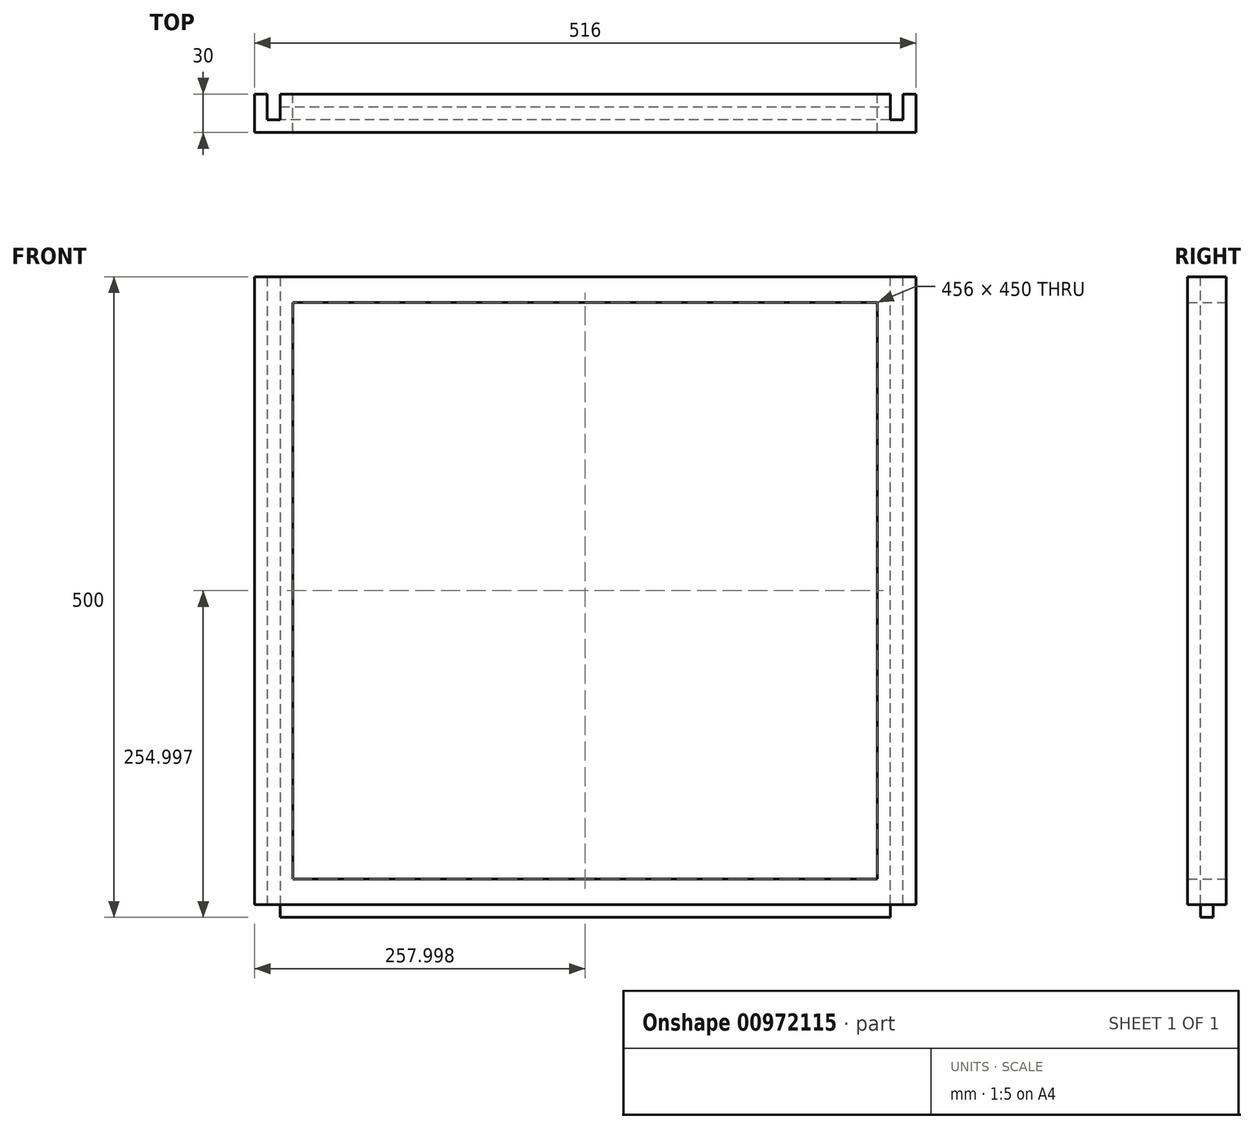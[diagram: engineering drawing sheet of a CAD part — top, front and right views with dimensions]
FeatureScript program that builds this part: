
annotation { "Feature Type Name" : "Feature", "Feature Type Description" : "" }
export const myFeature = defineFeature(function(context is Context, id is Id, definition is map)
    precondition{}
    {
        {
            var Q0;
            Q0=qCreatedBy(makeId("Front.planeOp"),FACE);
            var sketch = newSketch(context, id + "F0", { "sketchPlane" : qUnion([Q0])});
            skLineSegment(sketch, "E0.bottom", {"start": v(-276.65, 302.68) * mm, "end": v(259.35, 302.68) * mm});
            skLineSegment(sketch, "E0.top", {"start": v(-276.65, -197.32) * mm, "end": v(259.35, -197.32) * mm});
            skLineSegment(sketch, "E0.left", {"start": v(-276.65, 302.68) * mm, "end": v(-276.65, -197.32) * mm});
            skLineSegment(sketch, "E0.right", {"start": v(259.35, 302.68) * mm, "end": v(259.35, -197.32) * mm});
            skLineSegment(sketch, "E1.bottom", {"start": v(-236.65, -167.32) * mm, "end": v(219.35, -167.32) * mm});
            skLineSegment(sketch, "E1.top", {"start": v(-236.65, 282.68) * mm, "end": v(219.35, 282.68) * mm});
            skLineSegment(sketch, "E1.left", {"start": v(-236.65, -167.32) * mm, "end": v(-236.65, 282.68) * mm});
            skLineSegment(sketch, "E1.right", {"start": v(219.35, -167.32) * mm, "end": v(219.35, 282.68) * mm});
            skSolve(sketch);
        }
        {
            var Q0;
            Q0 = qSketchRegion(id + "F0", true);
            extrude(context, id + "F1", {"entities" : qUnion([Q0]), "depth" : 20 * mm, "offsetDistance" : 25 * mm});
        }
        {
            var Q0;
            Q0=makeQuery(id+"F1.opExtrude","SWEPT_FACE",FACE,{"disambiguationData":[OSD([sQuery(id+"F0.wireOp",EDGE,"E0.left")])]});
            var sketch = newSketch(context, id + "F2", { "sketchPlane" : qUnion([Q0])});
            skLineSegment(sketch, "E2.bottom", {"start": v(20, -197.32) * mm, "end": v(10, -197.32) * mm});
            skLineSegment(sketch, "E2.top", {"start": v(20, -187.32) * mm, "end": v(10, -187.32) * mm});
            skLineSegment(sketch, "E2.left", {"start": v(20, -197.32) * mm, "end": v(20, -187.32) * mm});
            skLineSegment(sketch, "E2.right", {"start": v(10, -197.32) * mm, "end": v(10, -187.32) * mm});
            skSolve(sketch);
        }
        {
            var Q0;
            Q0 = qSketchRegion(id + "F2", true);
            extrude(context, id + "F3", {"entities" : qUnion([Q0]), "operationType" : NewBodyOperationType.REMOVE, "endBound" : BoundingType.UP_TO_NEXT, "oppositeDirection" : true, "depth" : 25 * mm, "offsetDistance" : 25 * mm});
        }
        {
            var Q0;
            Q0=makeQuery(id+"F1.opExtrude","CAP_FACE",FACE,{"disambiguationData":[OSD([sQuery(id+"F0.wireOp",EDGE,"E0.bottom"),sQuery(id+"F0.wireOp",EDGE,"E0.top"),sQuery(id+"F0.wireOp",EDGE,"E0.left"),sQuery(id+"F0.wireOp",EDGE,"E0.right"),sQuery(id+"F0.wireOp",EDGE,"E1.bottom"),sQuery(id+"F0.wireOp",EDGE,"E1.top"),sQuery(id+"F0.wireOp",EDGE,"E1.left"),sQuery(id+"F0.wireOp",EDGE,"E1.right")])],"isStart":true});
            var sketch = newSketch(context, id + "F4", { "sketchPlane" : qUnion([Q0])});
            skLineSegment(sketch, "E3.bottom", {"start": v(246.65, 302.68) * mm, "end": v(256.65, 302.68) * mm});
            skLineSegment(sketch, "E3.top", {"start": v(246.65, -197.32) * mm, "end": v(256.65, -197.32) * mm});
            skLineSegment(sketch, "E3.left", {"start": v(246.65, 302.68) * mm, "end": v(246.65, -197.32) * mm});
            skLineSegment(sketch, "E3.right", {"start": v(256.65, 302.68) * mm, "end": v(256.65, -197.32) * mm});
            skLineSegment(sketch, "E4.bottom", {"start": v(-239.35, -197.32) * mm, "end": v(-229.35, -197.32) * mm});
            skLineSegment(sketch, "E4.top", {"start": v(-239.35, 302.68) * mm, "end": v(-229.35, 302.68) * mm});
            skLineSegment(sketch, "E4.left", {"start": v(-239.35, -197.32) * mm, "end": v(-239.35, 302.68) * mm});
            skLineSegment(sketch, "E4.right", {"start": v(-229.35, -197.32) * mm, "end": v(-229.35, 302.68) * mm});
            skSolve(sketch);
        }
        {
            var Q0;
            Q0 = qSketchRegion(id + "F4", true);
            extrude(context, id + "F5", {"entities" : qUnion([Q0]), "operationType" : NewBodyOperationType.REMOVE, "oppositeDirection" : true, "depth" : 10 * mm, "offsetDistance" : 25 * mm});
        }
        {
            var Q0;
            Q0=makeQuery(id+"F1.opExtrude","SWEPT_FACE",FACE,{"disambiguationData":[OSD([sQuery(id+"F0.wireOp",EDGE,"E0.right")])]});
            var sketch = newSketch(context, id + "F6", { "sketchPlane" : qUnion([Q0])});
            skLineSegment(sketch, "E5.bottom", {"start": v(-10, -197.32) * mm, "end": v(-10, -197.32) * mm});
            skPoint(sketch, "E6.oppositeSnap0", {"position": v(-15, -187.32) * mm});
            skLineSegment(sketch, "E6.bottom", {"start": v(-10, -197.32) * mm, "end": v(0, -197.32) * mm});
            skLineSegment(sketch, "E6.top", {"start": v(-10, -187.32) * mm, "end": v(0, -187.32) * mm});
            skLineSegment(sketch, "E6.left", {"start": v(-10, -197.32) * mm, "end": v(-10, -187.32) * mm});
            skLineSegment(sketch, "E6.right", {"start": v(0, -197.32) * mm, "end": v(0, -187.32) * mm});
            skSolve(sketch);
        }
        {
            var Q0;
            Q0=makeQuery(id+"F6.imprint","IMPRINT",FACE,{"disambiguationData":[TD([[makeQuery(id+"F6.imprint","IMPRINT",EDGE,{"derivedFrom":sQuery(id+"F6.wireOp",EDGE,"E6.bottom")}),1.0]])]});
            extrude(context, id + "F7", {"entities" : qUnion([Q0]), "operationType" : NewBodyOperationType.REMOVE, "endBound" : BoundingType.UP_TO_NEXT, "oppositeDirection" : true, "depth" : 25 * mm, "offsetDistance" : 25 * mm});
        }
        {
            var Q0;
            Q0=makeQuery(id+"F1.opExtrude","SWEPT_FACE",FACE,{"disambiguationData":[OSD([sQuery(id+"F0.wireOp",EDGE,"E0.left")])]});
            var sketch = newSketch(context, id + "F8", { "sketchPlane" : qUnion([Q0])});
            skLineSegment(sketch, "E7.bottom", {"start": v(10, -197.32) * mm, "end": v(0, -197.32) * mm});
            skLineSegment(sketch, "E7.top", {"start": v(10, -187.32) * mm, "end": v(0, -187.32) * mm});
            skLineSegment(sketch, "E7.left", {"start": v(10, -197.32) * mm, "end": v(10, -187.32) * mm});
            skLineSegment(sketch, "E7.right", {"start": v(0, -197.32) * mm, "end": v(0, -187.32) * mm});
            skSolve(sketch);
        }
        {
            var Q0;
            Q0=makeQuery(id+"F8.imprint","IMPRINT",FACE,{"disambiguationData":[TD([[makeQuery(id+"F8.imprint","IMPRINT",EDGE,{"derivedFrom":sQuery(id+"F8.wireOp",EDGE,"E7.bottom")}),-1.0]])]});
            extrude(context, id + "F9", {"entities" : qUnion([Q0]), "operationType" : NewBodyOperationType.REMOVE, "endBound" : BoundingType.UP_TO_NEXT, "oppositeDirection" : true, "depth" : 25 * mm, "offsetDistance" : 25 * mm});
        }
        {
            var Q0;
            Q0=makeQuery(id+"F1.opExtrude","SWEPT_FACE",FACE,{"disambiguationData":[OSD([sQuery(id+"F0.wireOp",EDGE,"E0.bottom")])]});
            var sketch = newSketch(context, id + "F10", { "sketchPlane" : qUnion([Q0])});
            skLineSegment(sketch, "E8.bottom", {"start": v(259.35, 0) * mm, "end": v(249.35, 0) * mm});
            skLineSegment(sketch, "E8.top", {"start": v(259.35, -20) * mm, "end": v(249.35, -20) * mm});
            skLineSegment(sketch, "E8.left", {"start": v(259.35, 0) * mm, "end": v(259.35, -20) * mm});
            skLineSegment(sketch, "E8.right", {"start": v(249.35, 0) * mm, "end": v(249.35, -20) * mm});
            skLineSegment(sketch, "E9.bottom", {"start": v(-276.65, 0) * mm, "end": v(-266.65, 0) * mm});
            skLineSegment(sketch, "E9.top", {"start": v(-276.65, -20) * mm, "end": v(-266.65, -20) * mm});
            skLineSegment(sketch, "E9.left", {"start": v(-276.65, 0) * mm, "end": v(-276.65, -20) * mm});
            skLineSegment(sketch, "E9.right", {"start": v(-266.65, 0) * mm, "end": v(-266.65, -20) * mm});
            skSolve(sketch);
        }
        {
            var Q0;
            Q0=makeQuery(id+"F10.imprint","IMPRINT",FACE,{"disambiguationData":[TD([[makeQuery(id+"F10.imprint","IMPRINT",EDGE,{"derivedFrom":sQuery(id+"F10.wireOp",EDGE,"E9.bottom")}),-1.0]])]});
            var Q1;
            Q1=makeQuery(id+"F10.imprint","IMPRINT",FACE,{"disambiguationData":[TD([[makeQuery(id+"F10.imprint","IMPRINT",EDGE,{"derivedFrom":sQuery(id+"F10.wireOp",EDGE,"E8.bottom")}),-1.0]])]});
            extrude(context, id + "F11", {"entities" : qUnion([Q0, Q1]), "operationType" : NewBodyOperationType.REMOVE, "endBound" : BoundingType.UP_TO_NEXT, "oppositeDirection" : true, "depth" : 25 * mm, "offsetDistance" : 25 * mm});
        }
        {
            var Q0;
            {var subQ0=sQuery(id+"F0.wireOp",EDGE,"E1.top");var subQ1=sQuery(id+"F0.wireOp",EDGE,"E1.bottom");var subQ2=sQuery(id+"F0.wireOp",EDGE,"E0.top");var subQ3=sQuery(id+"F0.wireOp",EDGE,"E0.bottom");var subQ4=sQuery(id+"F0.wireOp",EDGE,"E1.left");var subQ5=sQuery(id+"F0.wireOp",EDGE,"E1.right");Q0=makeQuery(id+"F5.boolean.opBoolean","SPLIT",FACE,{"disambiguationData":[TD([makeQuery(id+"F1.opExtrude","SWEPT_FACE",FACE,{"disambiguationData":[OSD([subQ1])]})])],"derivedFrom":makeQuery(id+"F1.opExtrude","CAP_FACE",FACE,{"disambiguationData":[OSD([subQ3,subQ2,sQuery(id+"F0.wireOp",EDGE,"E0.left"),sQuery(id+"F0.wireOp",EDGE,"E0.right"),subQ1,subQ0,subQ4,subQ5])],"isStart":true})});}
            var Q1;
            {var subQ0=sQuery(id+"F0.wireOp",EDGE,"E0.bottom");var subQ1=sQuery(id+"F0.wireOp",EDGE,"E0.right");var subQ2=sQuery(id+"F0.wireOp",EDGE,"E0.top");Q1=makeQuery(id+"F5.boolean.opBoolean","SPLIT",FACE,{"disambiguationData":[TD([makeQuery(id+"F1.opExtrude","SWEPT_FACE",FACE,{"disambiguationData":[OSD([subQ1])]})])],"derivedFrom":makeQuery(id+"F1.opExtrude","CAP_FACE",FACE,{"disambiguationData":[OSD([subQ0,subQ2,sQuery(id+"F0.wireOp",EDGE,"E0.left"),subQ1,sQuery(id+"F0.wireOp",EDGE,"E1.bottom"),sQuery(id+"F0.wireOp",EDGE,"E1.top"),sQuery(id+"F0.wireOp",EDGE,"E1.left"),sQuery(id+"F0.wireOp",EDGE,"E1.right")])],"isStart":true})});}
            var Q2;
            {var subQ0=sQuery(id+"F0.wireOp",EDGE,"E0.bottom");var subQ1=sQuery(id+"F0.wireOp",EDGE,"E0.top");var subQ2=sQuery(id+"F0.wireOp",EDGE,"E0.left");Q2=makeQuery(id+"F5.boolean.opBoolean","SPLIT",FACE,{"disambiguationData":[TD([makeQuery(id+"F1.opExtrude","SWEPT_FACE",FACE,{"disambiguationData":[OSD([subQ2])]})])],"derivedFrom":makeQuery(id+"F1.opExtrude","CAP_FACE",FACE,{"disambiguationData":[OSD([subQ0,subQ1,subQ2,sQuery(id+"F0.wireOp",EDGE,"E0.right"),sQuery(id+"F0.wireOp",EDGE,"E1.bottom"),sQuery(id+"F0.wireOp",EDGE,"E1.top"),sQuery(id+"F0.wireOp",EDGE,"E1.left"),sQuery(id+"F0.wireOp",EDGE,"E1.right")])],"isStart":true})});}
            extrude(context, id + "F12", {"entities" : qUnion([Q0, Q1, Q2]), "operationType" : NewBodyOperationType.ADD, "depth" : 10 * mm, "offsetDistance" : 25 * mm});
        }
        {
            var Q0;
            {var subQ0=sQuery(id+"F4.wireOp",EDGE,"E4.right");Q0=makeQuery(id+"F12.boolean.opBoolean","MERGE",FACE,{"derivedFrom":[makeQuery(id+"F5.boolean.opBoolean","COPY",FACE,{"derivedFrom":makeQuery(id+"F5.opExtrude","SWEPT_FACE",FACE,{"disambiguationData":[OSD([subQ0])]})}),makeQuery(id+"F12.opExtrude","SWEPT_FACE",FACE,{"disambiguationData":[OSD([subQ0])]})]});}
            var sketch = newSketch(context, id + "F13", { "sketchPlane" : qUnion([Q0])});
            skLineSegment(sketch, "E10.bottom", {"start": v(10, -197.32) * mm, "end": v(0, -197.32) * mm});
            skLineSegment(sketch, "E10.top", {"start": v(10, -187.32) * mm, "end": v(0, -187.32) * mm});
            skLineSegment(sketch, "E10.left", {"start": v(10, -197.32) * mm, "end": v(10, -187.32) * mm});
            skLineSegment(sketch, "E10.right", {"start": v(0, -197.32) * mm, "end": v(0, -187.32) * mm});
            skSolve(sketch);
        }
        {
            var Q0;
            Q0=makeQuery(id+"F13.imprint","IMPRINT",FACE,{"disambiguationData":[TD([[makeQuery(id+"F13.imprint","IMPRINT",EDGE,{"derivedFrom":sQuery(id+"F13.wireOp",EDGE,"E10.bottom")}),1.0]])]});
            extrude(context, id + "F14", {"entities" : qUnion([Q0]), "operationType" : NewBodyOperationType.REMOVE, "endBound" : BoundingType.UP_TO_NEXT, "oppositeDirection" : true, "depth" : 25 * mm, "offsetDistance" : 25 * mm});
        }
    });
